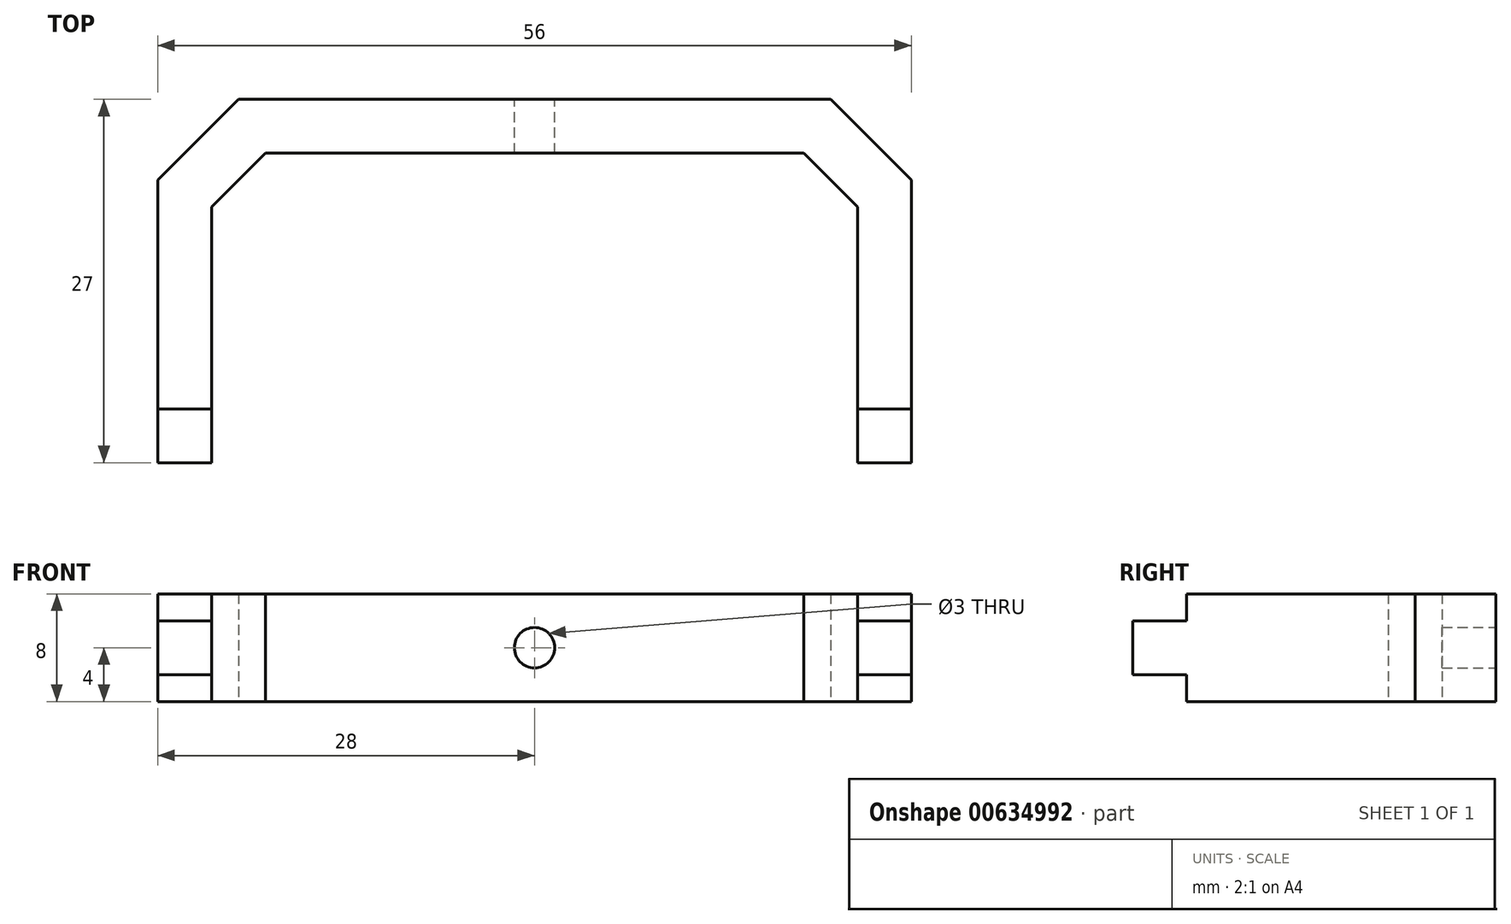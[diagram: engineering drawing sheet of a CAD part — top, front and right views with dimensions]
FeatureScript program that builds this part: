
annotation { "Feature Type Name" : "Feature", "Feature Type Description" : "" }
export const myFeature = defineFeature(function(context is Context, id is Id, definition is map)
    precondition{}
    {
        {
            var Q0;
            Q0=qCreatedBy(makeId("Top.planeOp"),FACE);
            var sketch = newSketch(context, id + "F0", { "sketchPlane" : qUnion([Q0])});
            skPoint(sketch, "E0.middle", {"position": v(0, 0) * mm});
            skPoint(sketch, "E1.endSnap0", {"position": v(-24, 0) * mm});
            skLineSegment(sketch, "E2", {"start": v(-28, -13.5) * mm, "end": v(-24, -13.5) * mm});
            skLineSegment(sketch, "E3", {"start": v(24, -13.5) * mm, "end": v(28, -13.5) * mm});
            skLineSegment(sketch, "E4", {"start": v(-24, 5.5) * mm, "end": v(-20, 9.5) * mm});
            skLineSegment(sketch, "E5", {"start": v(-24, 5.5) * mm, "end": v(-24, -13.5) * mm});
            skLineSegment(sketch, "E6", {"start": v(20, 9.5) * mm, "end": v(24, 5.5) * mm});
            skLineSegment(sketch, "E7", {"start": v(24, 5.5) * mm, "end": v(24, -13.5) * mm});
            skLineSegment(sketch, "E8", {"start": v(20, 9.5) * mm, "end": v(-20, 9.5) * mm});
            skLineSegment(sketch, "E9", {"start": v(-22, 13.5) * mm, "end": v(-28, 7.5) * mm});
            skPoint(sketch, "E9.startSnap0", {"position": v(-22, 7.5) * mm});
            skPoint(sketch, "E9.endSnap0", {"position": v(-22, 7.5) * mm});
            skPoint(sketch, "E10", {"position": v(22, 13.5) * mm});
            skPoint(sketch, "E11", {"position": v(-28, 13.5) * mm});
            skPoint(sketch, "E12", {"position": v(-28, 7.5) * mm});
            skLineSegment(sketch, "E13", {"start": v(22, 13.5) * mm, "end": v(28, 7.5) * mm});
            skLineSegment(sketch, "E14", {"start": v(-28, 7.5) * mm, "end": v(-28, -13.5) * mm});
            skLineSegment(sketch, "E15", {"start": v(-22, 13.5) * mm, "end": v(22, 13.5) * mm});
            skLineSegment(sketch, "E16", {"start": v(28, -13.5) * mm, "end": v(28, 7.5) * mm});
            skSolve(sketch);
        }
        {
            var Q0;
            Q0=makeQuery(id+"F0.imprint","IMPRINT",FACE,{"disambiguationData":[TD([[makeQuery(id+"F0.imprint","IMPRINT",EDGE,{"derivedFrom":sQuery(id+"F0.wireOp",EDGE,"E2")}),1.0]])]});
            extrude(context, id + "F1", {"entities" : qUnion([Q0]), "depth" : 8 * mm, "offsetDistance" : 25 * mm});
        }
        {
            var Q0;
            Q0=makeQuery(id+"F1.opExtrude","SWEPT_FACE",FACE,{"disambiguationData":[OSD([sQuery(id+"F0.wireOp",EDGE,"E16")])]});
            var sketch = newSketch(context, id + "F2", { "sketchPlane" : qUnion([Q0])});
            skLineSegment(sketch, "E17", {"start": v(-9.5, 6) * mm, "end": v(-13.5, 6) * mm});
            skLineSegment(sketch, "E18", {"start": v(-13.5, 2) * mm, "end": v(-9.5, 2) * mm});
            skLineSegment(sketch, "E19", {"start": v(-9.5, 8) * mm, "end": v(-9.5, 6) * mm});
            skLineSegment(sketch, "E20", {"start": v(-9.5, 2) * mm, "end": v(-9.5, 0) * mm});
            skSolve(sketch);
        }
        {
            var Q0;
            {var subQ0=sQuery(id+"F2.wireOp",EDGE,"E17");Q0=makeQuery(id+"F2.imprint","IMPRINT",FACE,{"disambiguationData":[TD([[makeQuery(id+"F2.imprint","IMPRINT",EDGE,{"derivedFrom":subQ0}),-1.0]])]});}
            var Q1;
            {var subQ0=sQuery(id+"F2.wireOp",EDGE,"E18");Q1=makeQuery(id+"F2.imprint","IMPRINT",FACE,{"disambiguationData":[TD([[makeQuery(id+"F2.imprint","IMPRINT",EDGE,{"derivedFrom":subQ0}),-1.0]])]});}
            extrude(context, id + "F3", {"entities" : qUnion([Q0, Q1]), "operationType" : NewBodyOperationType.REMOVE, "oppositeDirection" : true, "depth" : 4.2 * mm, "offsetDistance" : 25 * mm});
        }
        {
            var Q0;
            Q0=makeQuery(id+"F1.opExtrude","SWEPT_FACE",FACE,{"disambiguationData":[OSD([sQuery(id+"F0.wireOp",EDGE,"E14")])]});
            var sketch = newSketch(context, id + "F4", { "sketchPlane" : qUnion([Q0])});
            skLineSegment(sketch, "E21", {"start": v(9.5, 0) * mm, "end": v(9.5, 8) * mm, "construction": true});
            skLineSegment(sketch, "E22", {"start": v(9.5, 2) * mm, "end": v(13.5, 2) * mm});
            skLineSegment(sketch, "E23", {"start": v(9.5, 6) * mm, "end": v(13.5, 6) * mm});
            skLineSegment(sketch, "E24", {"start": v(9.5, 0) * mm, "end": v(9.5, 2) * mm});
            skLineSegment(sketch, "E25", {"start": v(9.5, 6) * mm, "end": v(9.5, 8) * mm});
            skSolve(sketch);
        }
        {
            var Q0;
            {var subQ0=sQuery(id+"F4.wireOp",EDGE,"E22");Q0=makeQuery(id+"F4.imprint","IMPRINT",FACE,{"disambiguationData":[TD([[makeQuery(id+"F4.imprint","IMPRINT",EDGE,{"derivedFrom":subQ0}),-1.0]])]});}
            var Q1;
            {var subQ0=sQuery(id+"F4.wireOp",EDGE,"E23");Q1=makeQuery(id+"F4.imprint","IMPRINT",FACE,{"disambiguationData":[TD([[makeQuery(id+"F4.imprint","IMPRINT",EDGE,{"derivedFrom":subQ0}),1.0]])]});}
            extrude(context, id + "F5", {"entities" : qUnion([Q0, Q1]), "operationType" : NewBodyOperationType.REMOVE, "oppositeDirection" : true, "depth" : 4.1 * mm, "offsetDistance" : 25 * mm});
        }
        {
            var Q0;
            Q0=makeQuery(id+"F1.opExtrude","SWEPT_FACE",FACE,{"disambiguationData":[OSD([sQuery(id+"F0.wireOp",EDGE,"E15")])]});
            var sketch = newSketch(context, id + "F6", { "sketchPlane" : qUnion([Q0])});
            skLineSegment(sketch, "E26", {"start": v(-22, 4) * mm, "end": v(22, 4) * mm, "construction": true});
            skLineSegment(sketch, "E27", {"start": v(0, 8) * mm, "end": v(0, 0) * mm, "construction": true});
            skPoint(sketch, "E28", {"position": v(0, 4) * mm});
            skCircle(sketch, "E29", {"center": v(0, 4) * mm, "radius": 1.5 * mm});
            skSolve(sketch);
        }
        {
            var Q0;
            Q0=makeQuery(id+"F6.imprint","IMPRINT",FACE,{"disambiguationData":[TD([[makeQuery(id+"F6.imprint","IMPRINT",EDGE,{"derivedFrom":sQuery(id+"F6.wireOp",EDGE,"E29")}),1.0]])]});
            extrude(context, id + "F7", {"entities" : qUnion([Q0]), "operationType" : NewBodyOperationType.REMOVE, "oppositeDirection" : true, "depth" : 5 * mm, "offsetDistance" : 25 * mm});
        }
    });
